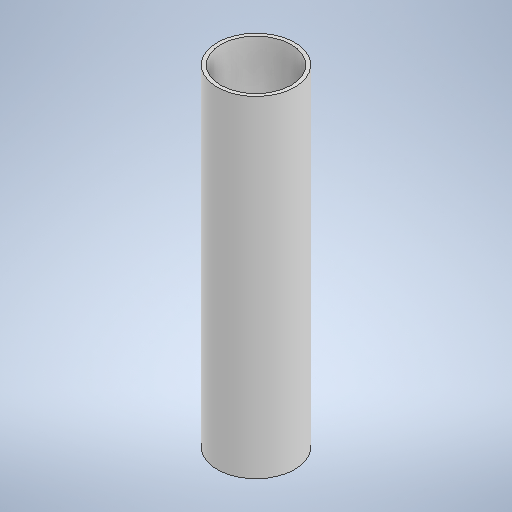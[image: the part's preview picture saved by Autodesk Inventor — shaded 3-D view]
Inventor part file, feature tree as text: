
AUTODESK INVENTOR PART (.ipt)
format: ipt  version: 2025.2 (Build 292293000, 293)  size: 226,304 bytes
history: native  units: mm
features: extrude x1, sketch x1
ambient origin geometry x8: Origin, YZ Plane, XZ Plane, XY Plane, X Axis, Y Axis, Z Axis, Center Point
bodies: Body1 (feature_tree)
feature tree (2):
  extrude  "Extrusion7"  Depth=94.0mm
  sketch  "Sketch7"  dims[d40=20.0mm d41=22.0mm d42=94.0mm d43=0.0mm]
